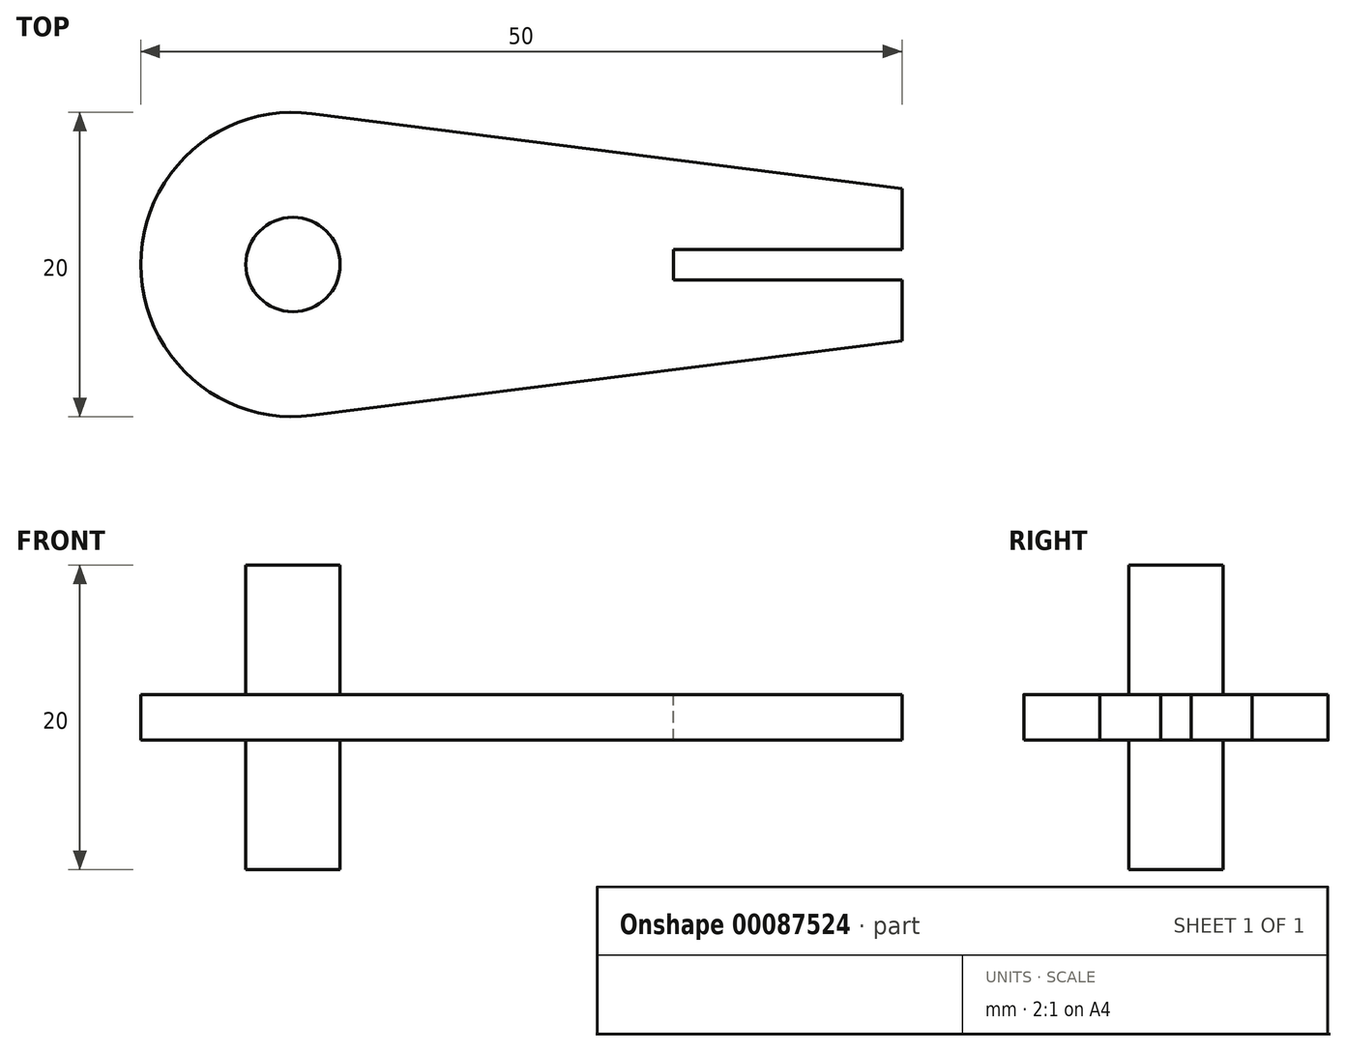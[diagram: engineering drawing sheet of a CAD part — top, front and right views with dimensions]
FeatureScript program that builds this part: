
annotation { "Feature Type Name" : "Feature", "Feature Type Description" : "" }
export const myFeature = defineFeature(function(context is Context, id is Id, definition is map)
    precondition{}
    {
        {
            var Q0;
            Q0=qCreatedBy(makeId("Top.planeOp"),FACE);
            var sketch = newSketch(context, id + "F0", { "sketchPlane" : qUnion([Q0])});
            skCircle(sketch, "E0", {"center": v(0, 0) * mm, "radius": 10 * mm});
            skCircle(sketch, "E1", {"center": v(0, 0) * mm, "radius": 3.1 * mm});
            skLineSegment(sketch, "E2", {"start": v(40, 5) * mm, "end": v(40, -5) * mm});
            skLineSegment(sketch, "E3", {"start": v(40, 5) * mm, "end": v(0, 10.08) * mm});
            skLineSegment(sketch, "E4", {"start": v(40, -5) * mm, "end": v(0, -10.08) * mm});
            skSolve(sketch);
        }
        {
            var Q0;
            Q0=makeQuery(id+"F0.imprint","IMPRINT",FACE,{"disambiguationData":[TD([[makeQuery(id+"F0.imprint","IMPRINT",EDGE,{"derivedFrom":sQuery(id+"F0.wireOp",EDGE,"E1")}),1.0]])]});
            extrude(context, id + "F1", {"entities" : qUnion([Q0]), "endBound" : BoundingType.SYMMETRIC, "depth" : 20 * mm});
        }
        {
            var Q0;
            Q0=makeQuery(id+"F0.imprint","IMPRINT",FACE,{"disambiguationData":[TD([[makeQuery(id+"F0.imprint","IMPRINT",EDGE,{"derivedFrom":sQuery(id+"F0.wireOp",EDGE,"E0")}),1.0]])]});
            var Q1;
            {var subQ0=sQuery(id+"F0.wireOp",EDGE,"7xwwVvcT-U73k-6AXb-dNko-pgiAhDf9KECB");var subQ1=sQuery(id+"F0.wireOp",EDGE,"E0");var subQ2=makeQuery(id+"F0.imprint","INTERSECT",VERTEX,{"disambiguationData":[OD(0.0)],"derivedFrom":[subQ1,subQ0]});Q1=makeQuery(id+"F0.imprint","IMPRINT",FACE,{"disambiguationData":[TD([[makeQuery(id+"F0.imprint","IMPRINT",EDGE,{"disambiguationData":[TD([[subQ2,1.0]])],"derivedFrom":subQ1}),1.0]])]});}
            var Q2;
            {var subQ0=sQuery(id+"F0.wireOp",EDGE,"gPXoG1VR-ffaB-TcTY-reCW-uO9KesnATeQA");var subQ1=sQuery(id+"F0.wireOp",EDGE,"E0");var subQ2=makeQuery(id+"F0.imprint","INTERSECT",VERTEX,{"disambiguationData":[OD(0.0)],"derivedFrom":[subQ1,subQ0]});Q2=makeQuery(id+"F0.imprint","IMPRINT",FACE,{"disambiguationData":[TD([[makeQuery(id+"F0.imprint","IMPRINT",EDGE,{"disambiguationData":[TD([[subQ2,-1.0]])],"derivedFrom":subQ1}),1.0]])]});}
            var Q3;
            {var subQ0=sQuery(id+"F0.wireOp",EDGE,"7xwwVvcT-U73k-6AXb-dNko-pgiAhDf9KECB");var subQ1=sQuery(id+"F0.wireOp",EDGE,"E0");var subQ2=makeQuery(id+"F0.imprint","INTERSECT",VERTEX,{"disambiguationData":[OD(1.0)],"derivedFrom":[subQ1,subQ0]});Q3=makeQuery(id+"F0.imprint","IMPRINT",FACE,{"disambiguationData":[TD([[makeQuery(id+"F0.imprint","IMPRINT",EDGE,{"disambiguationData":[TD([[subQ2,1.0]])],"derivedFrom":subQ1}),-1.0]])]});}
            extrude(context, id + "F2", {"entities" : qUnion([Q0, Q1, Q2, Q3]), "operationType" : NewBodyOperationType.ADD, "endBound" : BoundingType.SYMMETRIC, "depth" : 3 * mm});
        }
        {
            var Q0;
            Q0=makeQuery(id+"F2.opExtrude","CAP_FACE",FACE,{"disambiguationData":[OSD([sQuery(id+"F0.wireOp",EDGE,"E0"),sQuery(id+"F0.wireOp",EDGE,"E1"),sQuery(id+"F0.wireOp",EDGE,"gPXoG1VR-ffaB-TcTY-reCW-uO9KesnATeQA"),sQuery(id+"F0.wireOp",EDGE,"7xwwVvcT-U73k-6AXb-dNko-pgiAhDf9KECB")])],"isStart":false});
            var sketch = newSketch(context, id + "F3", { "sketchPlane" : qUnion([Q0])});
            skLineSegment(sketch, "E5.bottom", {"start": v(25, -1) * mm, "end": v(55, -1) * mm});
            skLineSegment(sketch, "E5.top", {"start": v(25, 1) * mm, "end": v(55, 1) * mm});
            skLineSegment(sketch, "E5.left", {"start": v(25, -1) * mm, "end": v(25, 1) * mm});
            skLineSegment(sketch, "E5.right", {"start": v(55, -1) * mm, "end": v(55, 1) * mm});
            skPoint(sketch, "E5.middle", {"position": v(40, 0) * mm});
            skSolve(sketch);
        }
        {
            var Q0;
            {var subQ5=sQuery(id+"F3.wireOp",EDGE,"E5.left");Q0=makeQuery(id+"F3.imprint","IMPRINT",FACE,{"disambiguationData":[TD([[makeQuery(id+"F3.imprint","IMPRINT",EDGE,{"derivedFrom":subQ5}),-1.0]])]});}
            extrude(context, id + "F4", {"entities" : qUnion([Q0]), "operationType" : NewBodyOperationType.REMOVE, "endBound" : BoundingType.THROUGH_ALL, "oppositeDirection" : true, "depth" : 25 * mm});
        }
    });
